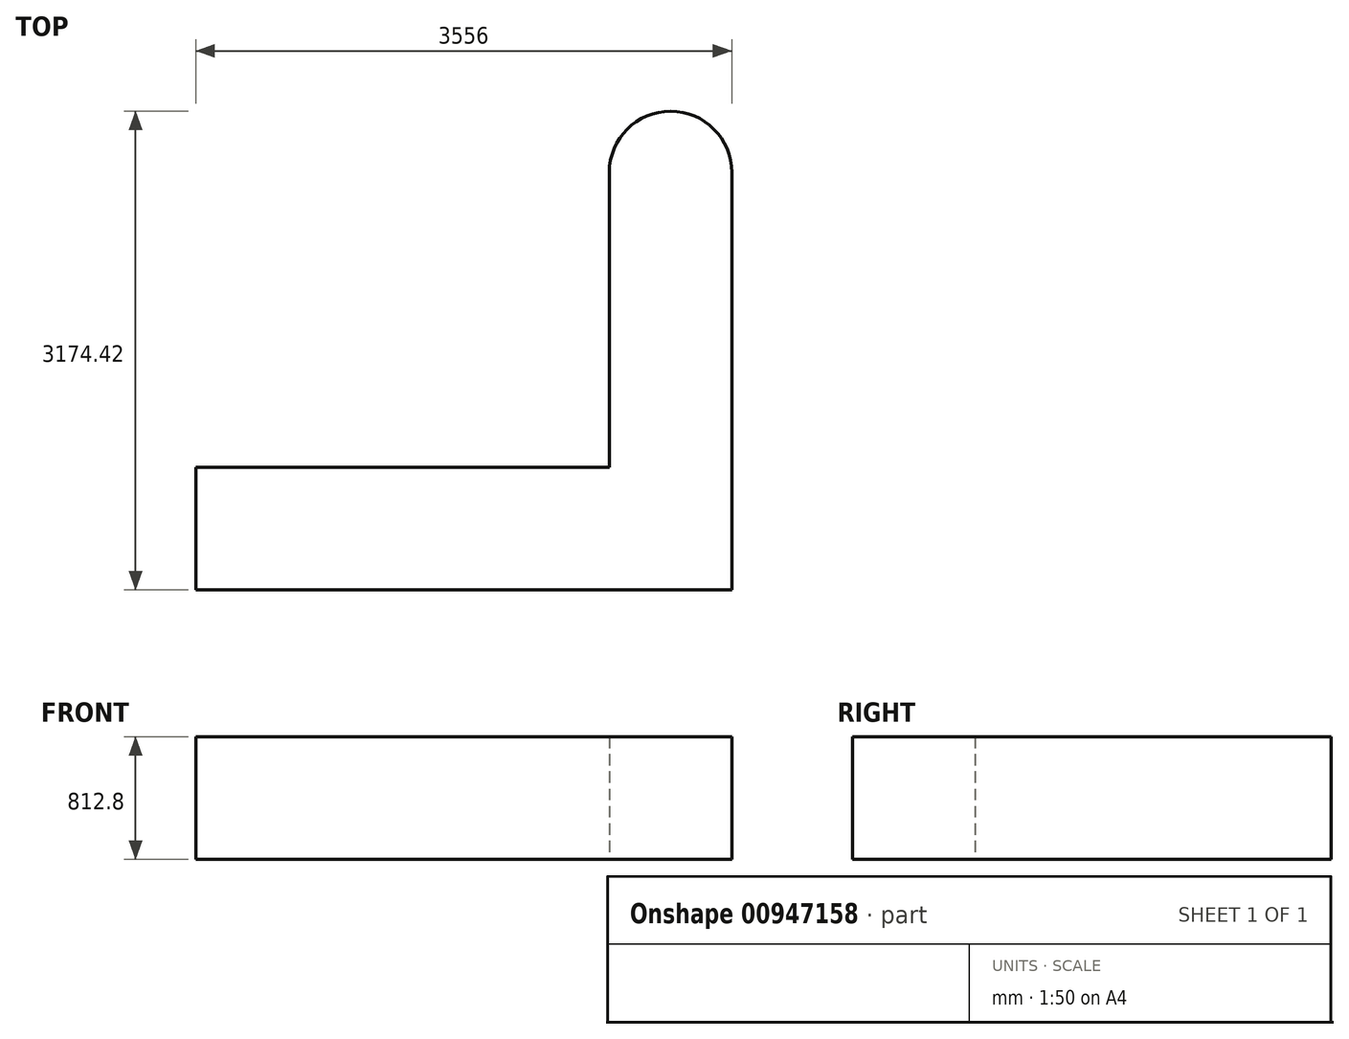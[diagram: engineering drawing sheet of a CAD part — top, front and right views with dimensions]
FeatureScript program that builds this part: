
annotation { "Feature Type Name" : "Feature", "Feature Type Description" : "" }
export const myFeature = defineFeature(function(context is Context, id is Id, definition is map)
    precondition{}
    {
        {
            var Q0;
            Q0=qCreatedBy(makeId("Top.planeOp"),FACE);
            var sketch = newSketch(context, id + "F0", { "sketchPlane" : qUnion([Q0])});
            skLineSegment(sketch, "E0.bottom", {"start": v(0, 0) * mm, "end": v(3556, 0) * mm});
            skLineSegment(sketch, "E0.top", {"start": v(0, 812.8) * mm, "end": v(2743.2, 812.8) * mm});
            skLineSegment(sketch, "E0.left", {"start": v(0, 0) * mm, "end": v(0, 812.8) * mm});
            skLineSegment(sketch, "E0.right", {"start": v(3556, 0) * mm, "end": v(3556, 812.8) * mm});
            skLineSegment(sketch, "E1.left", {"start": v(3556, 812.8) * mm, "end": v(3556, 2768.02) * mm});
            skLineSegment(sketch, "E1.right", {"start": v(2743.2, 812.8) * mm, "end": v(2743.2, 2768.02) * mm});
            skLineSegment(sketch, "E2", {"start": v(1066.8, 812.8) * mm, "end": v(1066.8, 0) * mm, "construction": true});
            skLineSegment(sketch, "E3", {"start": v(1447.8, 812.8) * mm, "end": v(1447.8, 0) * mm, "construction": true});
            skLineSegment(sketch, "E4", {"start": v(2260.6, 812.8) * mm, "end": v(2260.6, 0) * mm, "construction": true});
            skLineSegment(sketch, "E5", {"start": v(2743.2, 812.8) * mm, "end": v(3556, 812.8) * mm, "construction": true});
            skLineSegment(sketch, "E6", {"start": v(2743.2, 1117.6) * mm, "end": v(3556, 1117.6) * mm, "construction": true});
            skLineSegment(sketch, "E7", {"start": v(2743.2, 1625.6) * mm, "end": v(3556, 1625.6) * mm, "construction": true});
            skLineSegment(sketch, "E8", {"start": v(2743.2, 2286) * mm, "end": v(3556, 2286) * mm, "construction": true});
            skArc(sketch, "E9", {"start": v(3556, 2768.02) * mm, "mid": v(3149.6, 3174.42) * mm, "end": v(2743.2, 2768.02) * mm});
            skPoint(sketch, "E10.orphan", {"position": v(2743.2, 2794) * mm});
            skSolve(sketch);
        }
        {
            var Q0;
            Q0 = qSketchRegion(id + "F0", true);
            extrude(context, id + "F1", {"entities" : qUnion([Q0]), "depth" : 812.8 * mm, "offsetDistance" : 25.4 * mm});
        }
    });
